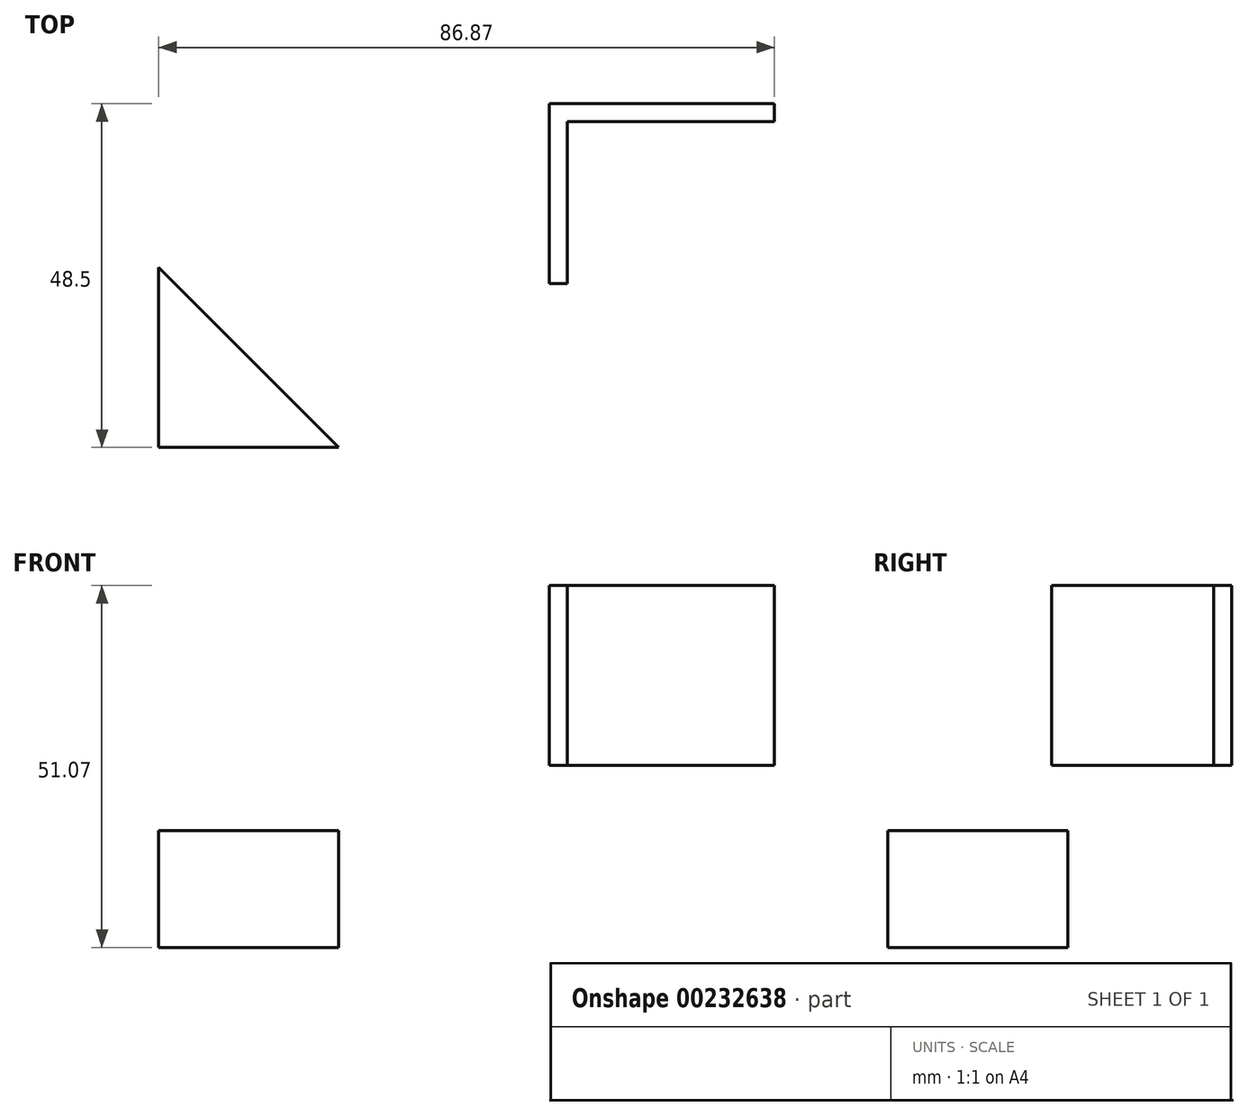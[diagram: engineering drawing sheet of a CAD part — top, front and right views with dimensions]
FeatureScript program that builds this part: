
annotation { "Feature Type Name" : "Feature", "Feature Type Description" : "" }
export const myFeature = defineFeature(function(context is Context, id is Id, definition is map)
    precondition{}
    {
        {
            var Q0;
            Q0=qCreatedBy(makeId("Front.planeOp"),FACE);
            var sketch = newSketch(context, id + "F0", { "sketchPlane" : qUnion([Q0])});
            skLineSegment(sketch, "E0.bottom", {"start": v(0, 32.02) * mm, "end": v(31.75, 32.02) * mm});
            skLineSegment(sketch, "E0.top", {"start": v(0, 6.62) * mm, "end": v(31.75, 6.62) * mm});
            skLineSegment(sketch, "E0.left", {"start": v(0, 32.02) * mm, "end": v(0, 6.62) * mm});
            skLineSegment(sketch, "E0.right", {"start": v(31.75, 32.02) * mm, "end": v(31.75, 6.62) * mm});
            skSolve(sketch);
        }
        {
            var Q0;
            Q0=makeQuery(id+"F0.imprint","IMPRINT",FACE,{"disambiguationData":[TD([[makeQuery(id+"F0.imprint","IMPRINT",EDGE,{"derivedFrom":sQuery(id+"F0.wireOp",EDGE,"E0.bottom")}),-1.0]])]});
            extrude(context, id + "F1", {"entities" : qUnion([Q0]), "depth" : 25.4 * mm});
        }
        {
            var Q0;
            Q0=makeQuery(id+"F1.opExtrude","CAP_FACE",FACE,{"disambiguationData":[OSD([sQuery(id+"F0.wireOp",EDGE,"E0.bottom"),sQuery(id+"F0.wireOp",EDGE,"E0.top"),sQuery(id+"F0.wireOp",EDGE,"E0.left"),sQuery(id+"F0.wireOp",EDGE,"E0.right")])],"isStart":false});
            var Q1;
            Q1=makeQuery(id+"F1.opExtrude","SWEPT_FACE",FACE,{"disambiguationData":[OSD([sQuery(id+"F0.wireOp",EDGE,"E0.right")])]});
            var Q2;
            Q2=makeQuery(id+"F1.opExtrude","SWEPT_FACE",FACE,{"disambiguationData":[OSD([sQuery(id+"F0.wireOp",EDGE,"E0.top")])]});
            var Q3;
            Q3=makeQuery(id+"F1.opExtrude","SWEPT_FACE",FACE,{"disambiguationData":[OSD([sQuery(id+"F0.wireOp",EDGE,"E0.bottom")])]});
            shell(context, id + "F2", {"entities" : qUnion([Q0, Q1, Q2, Q3]), "thickness" : 2.54 * mm});
        }
        {
            var Q0;
            Q0=qCreatedBy(makeId("Top.planeOp"),FACE);
            var sketch = newSketch(context, id + "F3", { "sketchPlane" : qUnion([Q0])});
            skLineSegment(sketch, "E1", {"start": v(-55.12, -48.5) * mm, "end": v(-55.12, -23.1) * mm});
            skLineSegment(sketch, "E2", {"start": v(-55.12, -48.5) * mm, "end": v(-29.72, -48.5) * mm});
            skLineSegment(sketch, "E3", {"start": v(-29.72, -48.5) * mm, "end": v(-55.12, -23.1) * mm});
            skSolve(sketch);
        }
        {
            var Q0;
            Q0=makeQuery(id+"F3.imprint","IMPRINT",FACE,{"disambiguationData":[TD([[makeQuery(id+"F3.imprint","IMPRINT",EDGE,{"derivedFrom":sQuery(id+"F3.wireOp",EDGE,"E1")}),-1.0]])]});
            extrude(context, id + "F4", {"entities" : qUnion([Q0]), "depth" : 19.05 * mm});
        }
        {
            var Q0;
            Q0=makeQuery(id+"F4.opExtrude","SWEPT_BODY",BODY,{"disambiguationData":[OSD([sQuery(id+"F3.wireOp",EDGE,"E1"),sQuery(id+"F3.wireOp",EDGE,"E2"),sQuery(id+"F3.wireOp",EDGE,"E3")])]});
            var Q1;
            Q1=makeQuery(id+"F4.opExtrude","SWEPT_EDGE",EDGE,{"disambiguationData":[OSD([sQuery(id+"F3.wireOp",EDGE,"E1"),sQuery(id+"F3.wireOp",EDGE,"E3")])]});
            transform(context, id + "F5", {"entities" : qUnion([Q0]), "transformType" : TransformType.TRANSLATION_ENTITY, "oppositeDirectionEntity" : false, "transformLine" : qUnion([Q1]), "makeCopy" : false});
        }
        {
            var Q0;
            Q0=makeQuery(id+"F4.opExtrude","CAP_FACE",FACE,{"disambiguationData":[OSD([sQuery(id+"F3.wireOp",EDGE,"E1"),sQuery(id+"F3.wireOp",EDGE,"E2"),sQuery(id+"F3.wireOp",EDGE,"E3")])],"isStart":false});
            extrude(context, id + "F6", {"entities" : qUnion([Q0]), "operationType" : NewBodyOperationType.REMOVE, "oppositeDirection" : true, "depth" : 2.54 * mm, "hasDraft" : true, "draftAngle" : 5 * degree});
        }
    });
